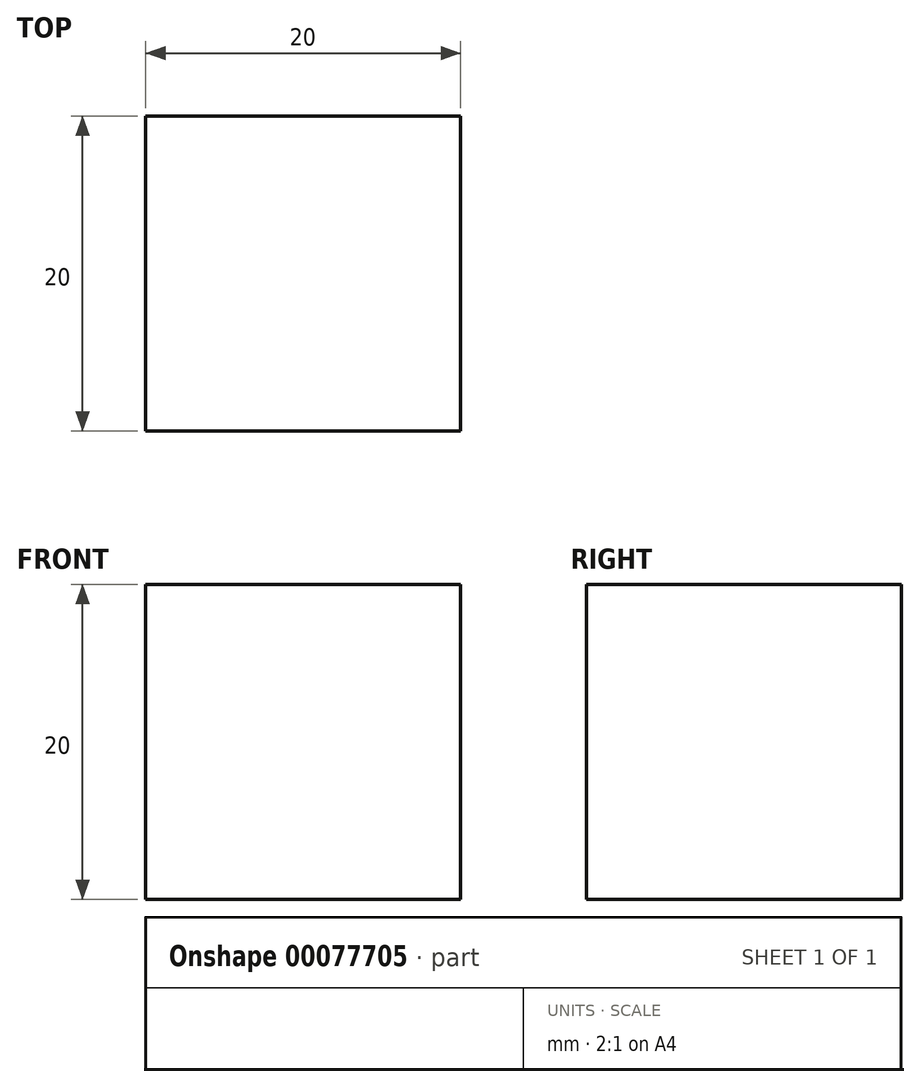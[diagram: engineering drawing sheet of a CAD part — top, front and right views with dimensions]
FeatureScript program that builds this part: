
annotation { "Feature Type Name" : "Feature", "Feature Type Description" : "" }
export const myFeature = defineFeature(function(context is Context, id is Id, definition is map)
    precondition{}
    {
        {
            var Q0;
            Q0=qCreatedBy(makeId("Top.planeOp"),FACE);
            var sketch = newSketch(context, id + "F0", { "sketchPlane" : qUnion([Q0])});
            skLineSegment(sketch, "E0.bottom", {"start": v(0, 20) * mm, "end": v(-20, 20) * mm});
            skLineSegment(sketch, "E0.top", {"start": v(0, 0) * mm, "end": v(-20, 0) * mm});
            skLineSegment(sketch, "E0.left", {"start": v(0, 20) * mm, "end": v(0, 0) * mm});
            skLineSegment(sketch, "E0.right", {"start": v(-20, 20) * mm, "end": v(-20, 0) * mm});
            skSolve(sketch);
        }
        {
            var Q0;
            Q0=makeQuery(id+"F0.imprint","IMPRINT",FACE,{"disambiguationData":[TD([[makeQuery(id+"F0.imprint","IMPRINT",EDGE,{"derivedFrom":sQuery(id+"F0.wireOp",EDGE,"E0.bottom")}),1.0]])]});
            extrude(context, id + "F1", {"entities" : qUnion([Q0]), "depth" : 20 * mm});
        }
    });
